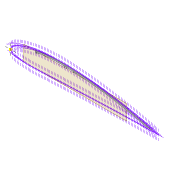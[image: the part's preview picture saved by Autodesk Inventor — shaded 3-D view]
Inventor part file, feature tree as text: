
AUTODESK INVENTOR PART (.ipt)
format: ipt  version: 2022 (Build 260153000, 153)  size: 477,184 bytes
history: native  units: mm
features: sketch x8, projected_geometry x8, extrude x7, shell x1, plane x1, chamfer x1
ambient origin geometry x8: Origin, YZ Plane, XZ Plane, XY Plane, X Axis, Y Axis, Z Axis, Center Point
bodies: Solid1 (feature_tree)
feature tree (26):
  extrude  "Extrusion1"  Depth=4.0mm
  shell  "Shell1"  Thickness=2.0mm
  extrude  "Extrusion8"  Depth=5.9mm
  extrude  "Extrusion3"  Depth=10.0mm TaperAngle=0.0deg
  extrude  "Extrusion4"  Depth=5.0mm
  extrude  "Extrusion5"  Depth=2.5mm
  plane  "Work Plane2"
  extrude  "Extrusion9"  Depth=5.0mm
  chamfer  "Chamfer1"  Distance=5.0mm
  extrude  "Extrusion11"  Depth=5.0mm TaperAngle=0.0deg
  sketch  "Sketch30"  dims[d40=2.5mm]
  sketch  "Sketch31"  dims[d62=72.0mm d63=5.0mm d64=2.0mm d65=0.0mm d66=2.5mm d67=12.0mm d68=75.0mm d69=20.0mm d70=0.5mm d71=10.0mm d72=0.0mm d75=3.0mm d76=3.0mm d77=2.0mm d78=45.0deg d79=0.0mm d80=1.0mm d81=1.0mm d82=1.0mm d83=1.0mm d84=1.0mm d85=10.0mm d86=0.0mm]
  sketch  "Sketch3"  dims[d0=2.0mm d1=0.0mm d2=4.0mm d7=2.0mm]
  sketch  "Sketch8"  dims[d8=2.0mm d9=5.9mm]
  sketch  "Sketch9"  dims[d13=10.0mm d14=0.0mm d16=10.0mm d17=0.0mm]
  projected_geometry  "Projected Loop4"
  projected_geometry  "Projected Loop10"
  sketch  "Sketch24"  dims[d22=2.0mm d23=0.0mm d32=5.0mm]
  projected_geometry  "Projected Loop11"
  projected_geometry  "Projected Loop12"
  sketch  "Sketch26"  dims[d34=1.6mm d35=2.5mm]
  projected_geometry  "Projected Loop13"
  sketch  "Sketch29"  dims[d37=5.0mm d38=1.6mm]
  projected_geometry  "Project Cut Edges1"
  projected_geometry  "Project Cut Edges2"
  projected_geometry  "Project Cut Edges3"
